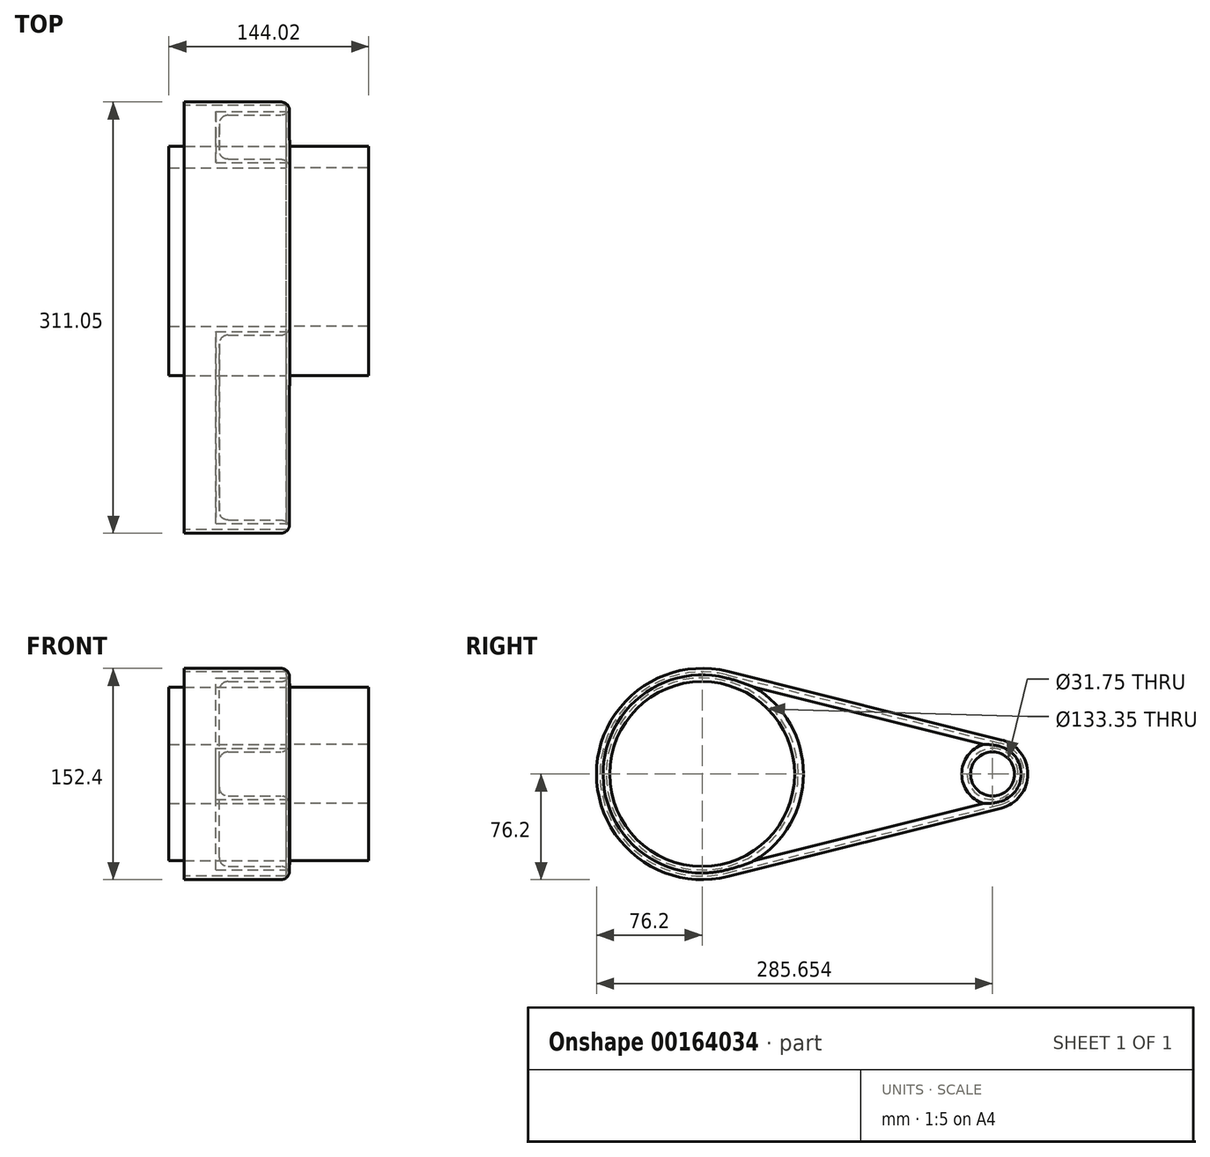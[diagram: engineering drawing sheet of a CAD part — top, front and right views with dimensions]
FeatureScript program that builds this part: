
annotation { "Feature Type Name" : "Feature", "Feature Type Description" : "" }
export const myFeature = defineFeature(function(context is Context, id is Id, definition is map)
    precondition{}
    {
        {
            var Q0;
            Q0=qCreatedBy(makeId("Right.planeOp"),FACE);
            var sketch = newSketch(context, id + "F0", { "sketchPlane" : qUnion([Q0])});
            skCircle(sketch, "E0", {"center": v(0, 0) * mm, "radius": 76.2 * mm});
            skCircle(sketch, "E1", {"center": v(209.45, 0) * mm, "radius": 25.4 * mm});
            skLineSegment(sketch, "E2", {"start": v(18.48, 73.92) * mm, "end": v(215.61, 24.64) * mm});
            skLineSegment(sketch, "E3", {"start": v(18.48, -73.92) * mm, "end": v(215.61, -24.64) * mm});
            skSolve(sketch);
        }
        {
            var Q0;
            {var subQ0=sQuery(id+"F0.wireOp",EDGE,"E0");var subQ1=makeQuery(id+"F0.imprint","INTERSECT",VERTEX,{"derivedFrom":[subQ0,sQuery(id+"F0.wireOp",EDGE,"E2")]});Q0=makeQuery(id+"F0.imprint","IMPRINT",FACE,{"disambiguationData":[TD([[makeQuery(id+"F0.imprint","IMPRINT",EDGE,{"disambiguationData":[TD([[subQ1,-1.0]])],"derivedFrom":subQ0}),1.0]])]});}
            var Q1;
            {var subQ0=sQuery(id+"F0.wireOp",EDGE,"E2");Q1=makeQuery(id+"F0.imprint","IMPRINT",FACE,{"disambiguationData":[TD([[makeQuery(id+"F0.imprint","IMPRINT",EDGE,{"derivedFrom":subQ0}),-1.0]])]});}
            var Q2;
            {var subQ0=sQuery(id+"F0.wireOp",EDGE,"E1");var subQ1=makeQuery(id+"F0.imprint","INTERSECT",VERTEX,{"derivedFrom":[subQ0,sQuery(id+"F0.wireOp",EDGE,"E2")]});Q2=makeQuery(id+"F0.imprint","IMPRINT",FACE,{"disambiguationData":[TD([[makeQuery(id+"F0.imprint","IMPRINT",EDGE,{"disambiguationData":[TD([[subQ1,-1.0]])],"derivedFrom":subQ0}),1.0]])]});}
            extrude(context, id + "F1", {"entities" : qUnion([Q0, Q1, Q2]), "depth" : 76.2 * mm});
        }
        {
            var Q0;
            Q0=makeQuery(id+"F1.opExtrude","CAP_FACE",FACE,{"disambiguationData":[OSD([sQuery(id+"F0.wireOp",EDGE,"E0"),sQuery(id+"F0.wireOp",EDGE,"E1"),sQuery(id+"F0.wireOp",EDGE,"E2"),sQuery(id+"F0.wireOp",EDGE,"E3")])],"isStart":false});
            var sketch = newSketch(context, id + "F2", { "sketchPlane" : qUnion([Q0])});
            skCircle(sketch, "E4", {"center": v(0, 0) * mm, "radius": 66.68 * mm});
            skCircle(sketch, "E5", {"center": v(209.45, 0) * mm, "radius": 15.88 * mm});
            skSolve(sketch);
        }
        {
            var Q0;
            Q0=makeQuery(id+"F2.imprint","IMPRINT",FACE,{"disambiguationData":[TD([[makeQuery(id+"F2.imprint","IMPRINT",EDGE,{"derivedFrom":sQuery(id+"F2.wireOp",EDGE,"E4")}),1.0]])]});
            var Q1;
            Q1=makeQuery(id+"F2.imprint","IMPRINT",FACE,{"disambiguationData":[TD([[makeQuery(id+"F2.imprint","IMPRINT",EDGE,{"derivedFrom":sQuery(id+"F2.wireOp",EDGE,"E5")}),1.0]])]});
            extrude(context, id + "F3", {"entities" : qUnion([Q0, Q1]), "operationType" : NewBodyOperationType.REMOVE, "oppositeDirection" : true, "depth" : 50.8 * mm});
        }
        {
            var Q0;
            Q0=makeQuery(id+"F1.opExtrude","CAP_FACE",FACE,{"disambiguationData":[OSD([sQuery(id+"F0.wireOp",EDGE,"E0"),sQuery(id+"F0.wireOp",EDGE,"E1"),sQuery(id+"F0.wireOp",EDGE,"E2"),sQuery(id+"F0.wireOp",EDGE,"E3")])],"isStart":true});
            shell(context, id + "F4", {"entities" : qUnion([Q0]), "thickness" : 2.54 * mm});
        }
        {
            var Q0;
            Q0=makeQuery(id+"F1.opExtrude","CAP_FACE",FACE,{"disambiguationData":[OSD([sQuery(id+"F0.wireOp",EDGE,"E0"),sQuery(id+"F0.wireOp",EDGE,"E1"),sQuery(id+"F0.wireOp",EDGE,"E2"),sQuery(id+"F0.wireOp",EDGE,"E3")])],"isStart":false});
            var Q1;
            Q1=makeQuery(id+"F3.boolean.opBoolean","COPY",EDGE,{"derivedFrom":makeQuery(id+"F3.opExtrude","CAP_EDGE",EDGE,{"disambiguationData":[OSD([sQuery(id+"F2.wireOp",EDGE,"E4")])],"isStart":false})});
            var Q2;
            Q2=makeQuery(id+"F3.boolean.opBoolean","COPY",EDGE,{"derivedFrom":makeQuery(id+"F3.opExtrude","CAP_EDGE",EDGE,{"disambiguationData":[OSD([sQuery(id+"F2.wireOp",EDGE,"E5")])],"isStart":false})});
            fillet(context, id + "F5", {"entities" : qUnion([Q0, Q1, Q2]), "radius" : 6.35 * mm, "tangentPropagation" : true, "allowEdgeOverflow" : false});
        }
        {
            var Q0;
            Q0=makeQuery(id+"F1.opExtrude","CAP_FACE",FACE,{"disambiguationData":[OSD([sQuery(id+"F0.wireOp",EDGE,"E0"),sQuery(id+"F0.wireOp",EDGE,"E1"),sQuery(id+"F0.wireOp",EDGE,"E2"),sQuery(id+"F0.wireOp",EDGE,"E3")])],"isStart":false});
            extrude(context, id + "F6", {"entities" : qUnion([Q0]), "operationType" : NewBodyOperationType.ADD, "depth" : 56.9 * mm});
        }
        {
            var Q0;
            Q0=makeQuery(id+"F6.opExtrude","CAP_FACE",FACE,{"disambiguationData":[OSD([sQuery(id+"F0.wireOp",EDGE,"E0"),sQuery(id+"F0.wireOp",EDGE,"E1"),sQuery(id+"F0.wireOp",EDGE,"E2"),sQuery(id+"F0.wireOp",EDGE,"E3")])],"isStart":false});
            extrude(context, id + "F7", {"entities" : qUnion([Q0]), "operationType" : NewBodyOperationType.ADD, "oppositeDirection" : true, "depth" : 144.02 * mm});
        }
    });
